# Revit family: Sluice Sink
name_source: partatom
category: Plumbing Fixtures
units: mm (PartAtom-declared; Revit-internal decimal feet)

## family parameters
Always vertical = Yes
Cut with Voids When Loaded = No
OmniClass Number = 23.45.00.00
OmniClass Title = Sanitary, Laundry, and Cleaning Equipment
Part Type = Normal
Room Calculation Point = No
Round Connector Dimension = Use Diameter
Shared = No
Work Plane-Based = No

## types (2) — shared parameters
Assembly = Pressed
Brand = Mercer
Description = NZ Made Flushing Rim Sluice Sink
Finish = Classic
Includes = 40mm Inlet
Material = 1.2mm 304 Stainless Steel
Model = Sluice Sink
Sink Material = Stainless Steel
Waste = Welded 75 or 100mm outlet
zero-valued in all types: Default Elevation

## per-type parameters (varying)
| type | FRSSWI100 | FRSSWI75 | Manufacturer |
| FRSSWI75 | No | Yes |  |
| FRSSWI100 | Yes | No | Mercer |

## geometry (parser evidence)
native form markers: Sweep x7
no freeform markers — native parametric forms only
